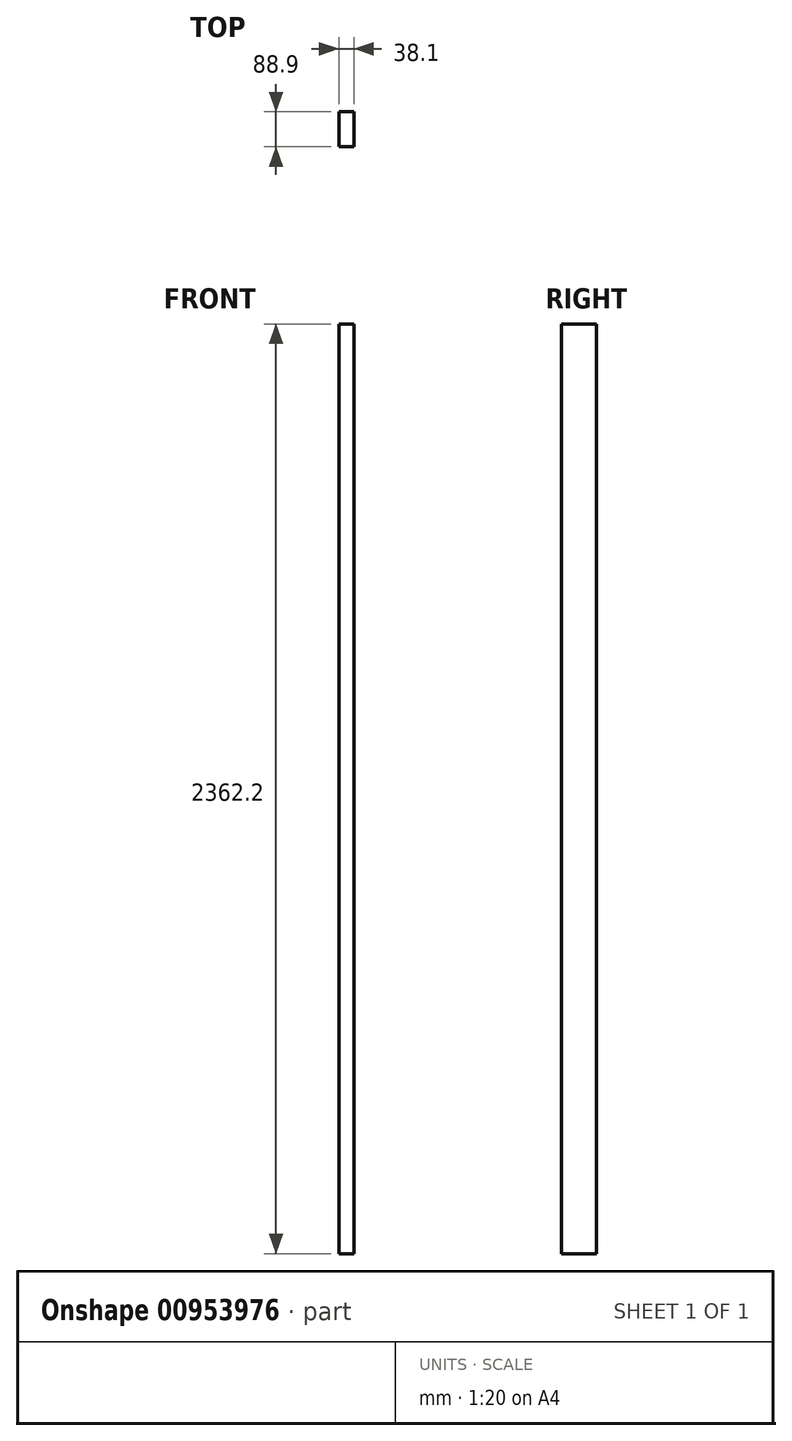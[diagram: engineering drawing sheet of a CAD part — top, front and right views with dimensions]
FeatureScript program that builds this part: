
annotation { "Feature Type Name" : "Feature", "Feature Type Description" : "" }
export const myFeature = defineFeature(function(context is Context, id is Id, definition is map)
    precondition{}
    {
        {
            var Q0;
            Q0=qCreatedBy(makeId("Top.planeOp"),FACE);
            var sketch = newSketch(context, id + "F0", { "sketchPlane" : qUnion([Q0])});
            skLineSegment(sketch, "E0.bottom", {"start": v(19.05, -44.45) * mm, "end": v(-19.05, -44.45) * mm});
            skLineSegment(sketch, "E0.top", {"start": v(19.05, 44.45) * mm, "end": v(-19.05, 44.45) * mm});
            skLineSegment(sketch, "E0.left", {"start": v(19.05, -44.45) * mm, "end": v(19.05, 44.45) * mm});
            skLineSegment(sketch, "E0.right", {"start": v(-19.05, -44.45) * mm, "end": v(-19.05, 44.45) * mm});
            skPoint(sketch, "E0.middle", {"position": v(0, 0) * mm});
            skSolve(sketch);
        }
        {
            var Q0;
            Q0=qSketchRegion(id+"F0",true);
            extrude(context, id + "F1", {"entities" : qUnion([Q0]), "depth" : 2362.2 * mm, "offsetDistance" : 25.4 * mm});
        }
    });
